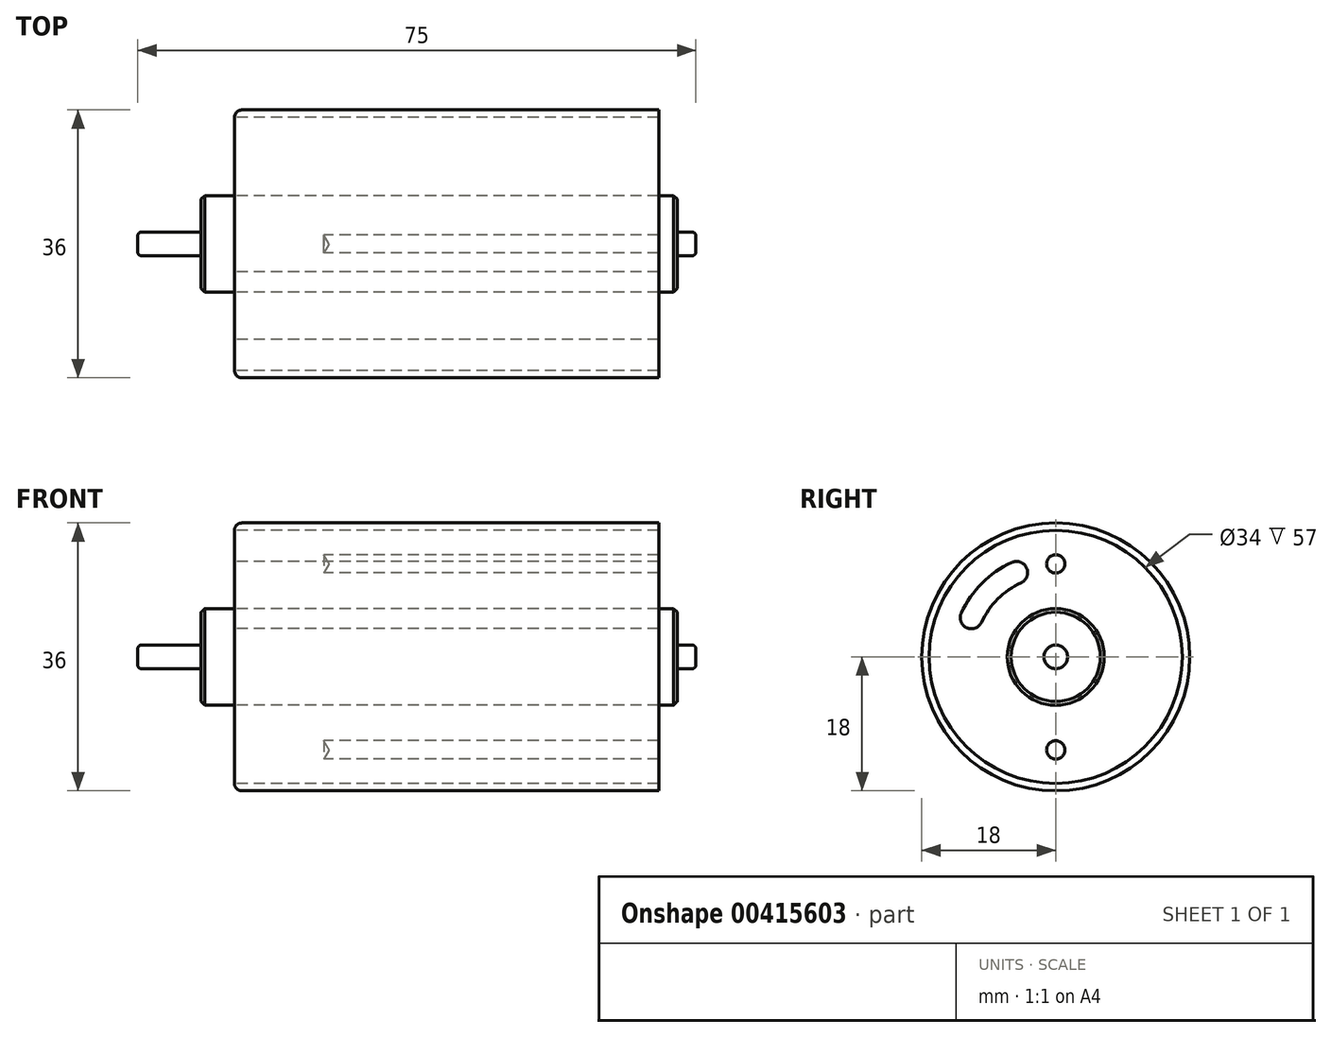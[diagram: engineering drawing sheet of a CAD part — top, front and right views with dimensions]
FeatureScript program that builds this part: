
annotation { "Feature Type Name" : "Feature", "Feature Type Description" : "" }
export const myFeature = defineFeature(function(context is Context, id is Id, definition is map)
    precondition{}
    {
        {
            var Q0;
            Q0=qCreatedBy(makeId("Front.planeOp"),FACE);
            var sketch = newSketch(context, id + "F0", { "sketchPlane" : qUnion([Q0])});
            skLineSegment(sketch, "E0", {"start": v(-13, 0) * mm, "end": v(62, 0) * mm, "construction": true});
            skLineSegment(sketch, "E1", {"start": v(-13, 0) * mm, "end": v(-13, 1.58) * mm});
            skLineSegment(sketch, "E2", {"start": v(-13, 1.58) * mm, "end": v(-4.5, 1.58) * mm});
            skLineSegment(sketch, "E3", {"start": v(-4.5, 1.58) * mm, "end": v(-4.5, 6.5) * mm});
            skLineSegment(sketch, "E4", {"start": v(-4.5, 6.5) * mm, "end": v(0, 6.5) * mm});
            skLineSegment(sketch, "E5", {"start": v(0, 6.5) * mm, "end": v(0, 18) * mm});
            skLineSegment(sketch, "E6", {"start": v(0, 18) * mm, "end": v(57, 18) * mm});
            skLineSegment(sketch, "E7", {"start": v(57, 18) * mm, "end": v(57, 6.5) * mm});
            skLineSegment(sketch, "E8", {"start": v(57, 6.5) * mm, "end": v(59.5, 6.5) * mm});
            skLineSegment(sketch, "E9", {"start": v(59.5, 6.5) * mm, "end": v(59.5, 1.58) * mm});
            skLineSegment(sketch, "E10", {"start": v(59.5, 1.59) * mm, "end": v(62, 1.59) * mm});
            skLineSegment(sketch, "E11", {"start": v(62, 1.59) * mm, "end": v(62, 0) * mm});
            skLineSegment(sketch, "E12", {"start": v(-13, 0) * mm, "end": v(62, 0) * mm});
            skSolve(sketch);
        }
        {
            var Q0;
            Q0=makeQuery(id+"F0.imprint","IMPRINT",FACE,{"disambiguationData":[TD([[makeQuery(id+"F0.imprint","IMPRINT",EDGE,{"derivedFrom":sQuery(id+"F0.wireOp",EDGE,"E1")}),-1.0]])]});
            var Q1;
            Q1=sQuery(id+"F0.wireOp",EDGE,"E0");
            revolve(context, id + "F1", {"entities" : qUnion([Q0]), "axis" : qUnion([Q1]), "revolveType" : RevolveType.FULL});
        }
        {
            var Q0;
            Q0=makeQuery(id+"F1.opRevolve","SWEPT_FACE",FACE,{"disambiguationData":[OSD([sQuery(id+"F0.wireOp",EDGE,"E7")])]});
            var sketch = newSketch(context, id + "F2", { "sketchPlane" : qUnion([Q0])});
            skLineSegment(sketch, "E13.bottom", {"start": v(1.95, 14.5) * mm, "end": v(-1.95, 14.5) * mm});
            skLineSegment(sketch, "E13.top", {"start": v(1.95, 14) * mm, "end": v(-1.95, 14) * mm});
            skLineSegment(sketch, "E13.left", {"start": v(1.95, 14.5) * mm, "end": v(1.95, 14) * mm});
            skLineSegment(sketch, "E13.right", {"start": v(-1.95, 14.5) * mm, "end": v(-1.95, 14) * mm});
            skPoint(sketch, "E13.middle", {"position": v(0, 14.25) * mm});
            skLineSegment(sketch, "E14", {"start": v(-10, 0) * mm, "end": v(10, 0) * mm, "construction": true});
            skSolve(sketch);
        }
        {
            var Q0;
            Q0=makeQuery(id+"F2.imprint","IMPRINT",FACE,{"disambiguationData":[TD([[makeQuery(id+"F2.imprint","IMPRINT",EDGE,{"derivedFrom":sQuery(id+"F2.wireOp",EDGE,"E13.bottom")}),1.0]])]});
            extrude(context, id + "F3", {"entities" : qUnion([Q0]), "operationType" : NewBodyOperationType.ADD, "depth" : 5.5 * mm});
        }
        {
            var Q0;
            Q0=makeQuery(id+"F3.opExtrude","CAP_EDGE",EDGE,{"disambiguationData":[OSD([sQuery(id+"F2.wireOp",EDGE,"E13.right")])],"isStart":false});
            var Q1;
            Q1=makeQuery(id+"F3.opExtrude","CAP_EDGE",EDGE,{"disambiguationData":[OSD([sQuery(id+"F2.wireOp",EDGE,"E13.left")])],"isStart":false});
            chamfer(context, id + "F4", {"entities" : qUnion([Q0, Q1]), "width" : 1 * mm, "tangentPropagation" : true});
        }
        {
            var Q0;
            Q0=makeQuery(id+"F3.opExtrude","SWEPT_FACE",FACE,{"disambiguationData":[OSD([sQuery(id+"F2.wireOp",EDGE,"E13.bottom")])]});
            var sketch = newSketch(context, id + "F5", { "sketchPlane" : qUnion([Q0])});
            skPoint(sketch, "E15", {"position": v(60.5, 0) * mm});
            skSolve(sketch);
        }
        {
            var Q0;
            Q0=sQuery(id+"F5.wireOp",VERTEX,"E15");
            var Q1;
            Q1=makeQuery(id+"F1.opRevolve","SWEPT_BODY",BODY,{"disambiguationData":[OSD([sQuery(id+"F0.wireOp",EDGE,"E1"),sQuery(id+"F0.wireOp",EDGE,"E2"),sQuery(id+"F0.wireOp",EDGE,"E3"),sQuery(id+"F0.wireOp",EDGE,"E4"),sQuery(id+"F0.wireOp",EDGE,"E5"),sQuery(id+"F0.wireOp",EDGE,"E6"),sQuery(id+"F0.wireOp",EDGE,"E7"),sQuery(id+"F0.wireOp",EDGE,"E8"),sQuery(id+"F0.wireOp",EDGE,"E9"),sQuery(id+"F0.wireOp",EDGE,"E10"),sQuery(id+"F0.wireOp",EDGE,"E11"),sQuery(id+"F0.wireOp",EDGE,"E12")])]});
            hole(context, id + "F6", {"style" : HoleStyle.SIMPLE, "endStyle" : HoleEndStyle.BLIND, "holeDiameter" : 2 * mm, "holeDepth" : 12 * mm, "isTappedThrough" : true, "tappedDepth" : 12 * mm, "tapClearance" : 3, "locations" : qUnion([Q0]), "scope" : qUnion([Q1])});
        }
        {
            var Q0;
            Q0=makeQuery(id+"F1.opRevolve","SWEPT_FACE",FACE,{"disambiguationData":[OSD([sQuery(id+"F0.wireOp",EDGE,"E5")])]});
            var sketch = newSketch(context, id + "F7", { "sketchPlane" : qUnion([Q0])});
            skPoint(sketch, "E16", {"position": v(0, 12.5) * mm});
            skPoint(sketch, "E17", {"position": v(0, -12.5) * mm});
            skSolve(sketch);
        }
        {
            var Q0;
            Q0=makeQuery(id+"F1.opRevolve","SWEPT_EDGE",EDGE,{"disambiguationData":[OSD([sQuery(id+"F0.wireOp",EDGE,"E5"),sQuery(id+"F0.wireOp",EDGE,"E6")])]});
            fillet(context, id + "F8", {"entities" : qUnion([Q0]), "radius" : 1 * mm, "tangentPropagation" : true, "allowEdgeOverflow" : false});
        }
        {
            var Q0;
            Q0=makeQuery(id+"F1.opRevolve","SWEPT_EDGE",EDGE,{"disambiguationData":[OSD([sQuery(id+"F0.wireOp",EDGE,"E1"),sQuery(id+"F0.wireOp",EDGE,"E2")])]});
            var Q1;
            Q1=makeQuery(id+"F1.opRevolve","SWEPT_EDGE",EDGE,{"disambiguationData":[OSD([sQuery(id+"F0.wireOp",EDGE,"E10"),sQuery(id+"F0.wireOp",EDGE,"E11")])]});
            fillet(context, id + "F9", {"entities" : qUnion([Q0, Q1]), "radius" : .5 * mm, "tangentPropagation" : true, "allowEdgeOverflow" : false});
        }
        {
            var Q0;
            Q0=makeQuery(id+"F1.opRevolve","SWEPT_EDGE",EDGE,{"disambiguationData":[OSD([sQuery(id+"F0.wireOp",EDGE,"E8"),sQuery(id+"F0.wireOp",EDGE,"E9")])]});
            var Q1;
            Q1=makeQuery(id+"F1.opRevolve","SWEPT_EDGE",EDGE,{"disambiguationData":[OSD([sQuery(id+"F0.wireOp",EDGE,"E3"),sQuery(id+"F0.wireOp",EDGE,"E4")])]});
            chamfer(context, id + "F10", {"entities" : qUnion([Q0, Q1]), "width" : .5 * mm, "tangentPropagation" : true});
        }
        {
            var Q0;
            Q0=sQuery(id+"F7.wireOp",VERTEX,"E16");
            var Q1;
            Q1=sQuery(id+"F7.wireOp",VERTEX,"E17");
            var Q2;
            Q2=makeQuery(id+"F1.opRevolve","SWEPT_BODY",BODY,{"disambiguationData":[OSD([sQuery(id+"F0.wireOp",EDGE,"E1"),sQuery(id+"F0.wireOp",EDGE,"E2"),sQuery(id+"F0.wireOp",EDGE,"E3"),sQuery(id+"F0.wireOp",EDGE,"E4"),sQuery(id+"F0.wireOp",EDGE,"E5"),sQuery(id+"F0.wireOp",EDGE,"E6"),sQuery(id+"F0.wireOp",EDGE,"E7"),sQuery(id+"F0.wireOp",EDGE,"E8"),sQuery(id+"F0.wireOp",EDGE,"E9"),sQuery(id+"F0.wireOp",EDGE,"E10"),sQuery(id+"F0.wireOp",EDGE,"E11"),sQuery(id+"F0.wireOp",EDGE,"E12")])]});
            hole(context, id + "F11", {"style" : HoleStyle.SIMPLE, "endStyle" : HoleEndStyle.BLIND, "holeDiameter" : 2.46 * mm, "holeDepth" : 12 * mm, "isTappedThrough" : true, "tappedDepth" : 12 * mm, "tapClearance" : 3, "locations" : qUnion([Q0, Q1]), "scope" : qUnion([Q2])});
        }
        {
            var Q0;
            Q0=makeQuery(id+"F1.opRevolve","SWEPT_FACE",FACE,{"disambiguationData":[OSD([sQuery(id+"F0.wireOp",EDGE,"E5")])]});
            var sketch = newSketch(context, id + "F12", { "sketchPlane" : qUnion([Q0])});
            skArc(sketch, "E18", {"start": v(5.28, 11.33) * mm, "mid": v(8.84, 8.84) * mm, "end": v(11.33, 5.28) * mm});
            skLineSegment(sketch, "E19", {"start": v(0, 0) * mm, "end": v(8.84, 8.84) * mm, "construction": true});
            skLineSegment(sketch, "E20", {"start": v(0, 0) * mm, "end": v(5.28, 11.33) * mm, "construction": true});
            skLineSegment(sketch, "E21", {"start": v(0, 0) * mm, "end": v(11.33, 5.28) * mm, "construction": true});
            skArc(sketch, "E22.0.startCap", {"start": v(4.65, 9.97) * mm, "mid": v(3.92, 11.96) * mm, "end": v(5.92, 12.69) * mm});
            skArc(sketch, "E22.0.endCap", {"start": v(12.69, 5.92) * mm, "mid": v(11.96, 3.92) * mm, "end": v(9.97, 4.65) * mm});
            skArc(sketch, "E22.0.left", {"start": v(5.92, 12.69) * mm, "mid": v(9.9, 9.9) * mm, "end": v(12.69, 5.92) * mm});
            skArc(sketch, "E22.0.right", {"start": v(4.65, 9.97) * mm, "mid": v(7.78, 7.78) * mm, "end": v(9.97, 4.65) * mm});
            skSolve(sketch);
        }
        {
            var Q0;
            Q0=makeQuery(id+"F12.imprint","IMPRINT",FACE,{"disambiguationData":[TD([[makeQuery(id+"F12.imprint","IMPRINT",EDGE,{"derivedFrom":sQuery(id+"F12.wireOp",EDGE,"E22.0.startCap")}),-1.0]])]});
            extrude(context, id + "F13", {"entities" : qUnion([Q0]), "operationType" : NewBodyOperationType.REMOVE, "endBound" : BoundingType.UP_TO_NEXT, "oppositeDirection" : true, "depth" : 25 * mm});
        }
    });
